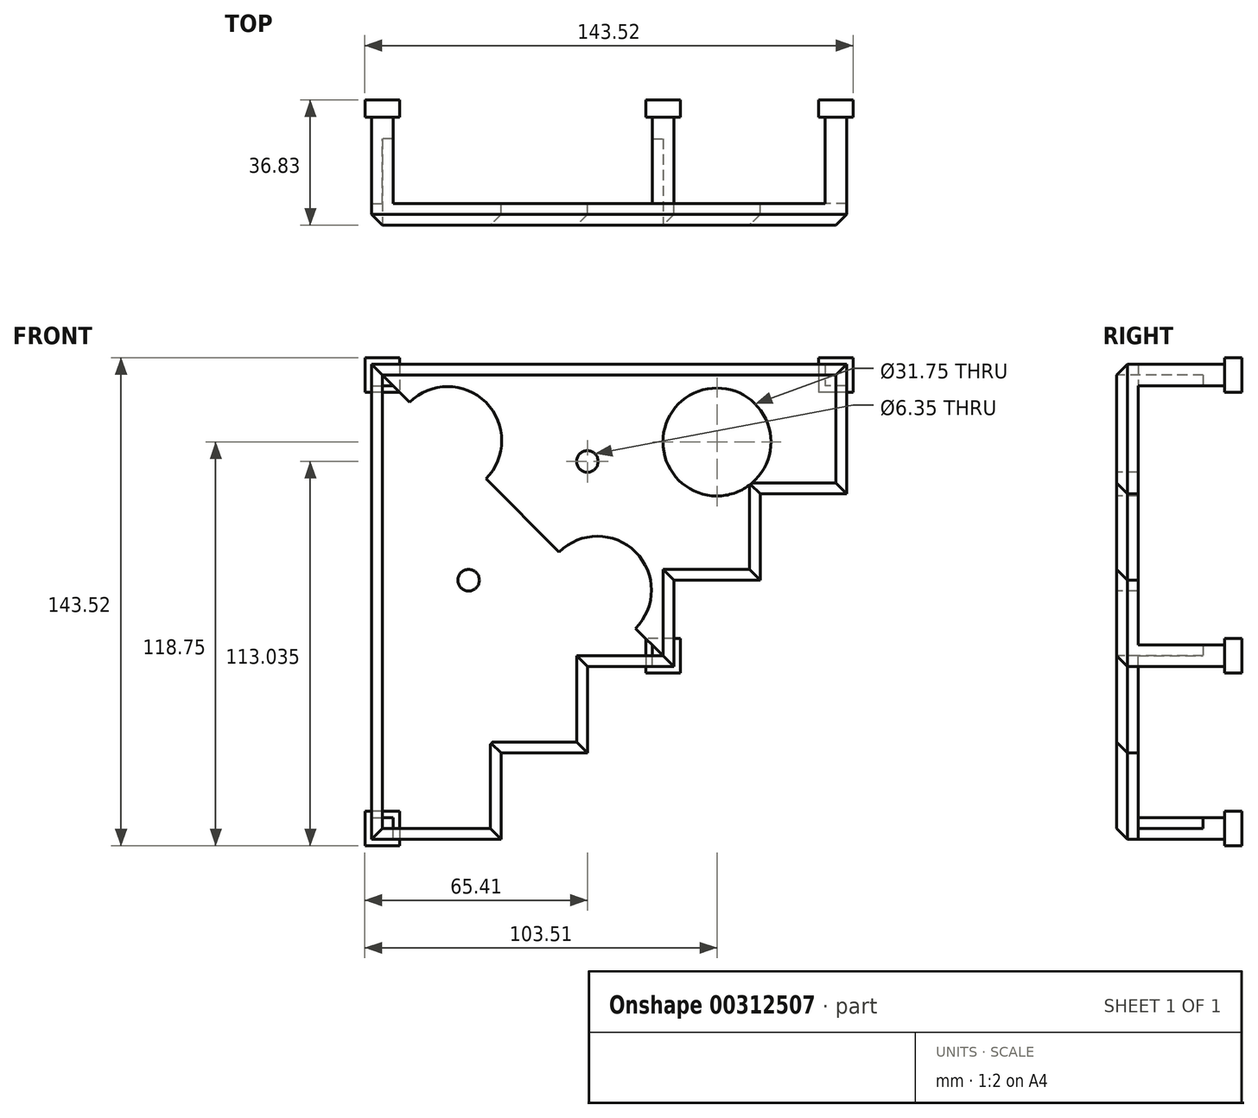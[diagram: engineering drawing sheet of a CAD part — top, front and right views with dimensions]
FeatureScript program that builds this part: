
annotation { "Feature Type Name" : "Feature", "Feature Type Description" : "" }
export const myFeature = defineFeature(function(context is Context, id is Id, definition is map)
    precondition{}
    {
        {
            var Q0;
            Q0=qCreatedBy(makeId("Front.planeOp"),FACE);
            var sketch = newSketch(context, id + "F0", { "sketchPlane" : qUnion([Q0])});
            skLineSegment(sketch, "E0", {"start": v(0, 0) * mm, "end": v(139.7, 0) * mm});
            skLineSegment(sketch, "E1", {"start": v(0, 0) * mm, "end": v(0, -139.7) * mm});
            skLineSegment(sketch, "E2", {"start": v(0, -139.7) * mm, "end": v(38.1, -139.7) * mm});
            skLineSegment(sketch, "E3", {"start": v(38.1, -139.7) * mm, "end": v(38.1, -114.3) * mm});
            skLineSegment(sketch, "E4", {"start": v(38.1, -114.3) * mm, "end": v(63.5, -114.3) * mm});
            skLineSegment(sketch, "E5", {"start": v(139.7, 0) * mm, "end": v(139.7, -38.1) * mm});
            skLineSegment(sketch, "E6", {"start": v(139.7, -38.1) * mm, "end": v(114.3, -38.1) * mm});
            skLineSegment(sketch, "E7", {"start": v(114.3, -38.1) * mm, "end": v(114.3, -63.5) * mm});
            skLineSegment(sketch, "E8", {"start": v(114.3, -63.5) * mm, "end": v(88.9, -63.5) * mm});
            skLineSegment(sketch, "E9", {"start": v(63.5, -114.3) * mm, "end": v(63.5, -88.9) * mm});
            skLineSegment(sketch, "E10", {"start": v(63.5, -88.9) * mm, "end": v(88.9, -88.9) * mm});
            skLineSegment(sketch, "E11", {"start": v(88.9, -88.9) * mm, "end": v(88.9, -63.5) * mm});
            skSolve(sketch);
        }
        {
            var Q0;
            Q0=makeQuery(id+"F0.imprint","IMPRINT",FACE,{"disambiguationData":[TD([[makeQuery(id+"F0.imprint","IMPRINT",EDGE,{"derivedFrom":sQuery(id+"F0.wireOp",EDGE,"E0")}),-1.0]])]});
            extrude(context, id + "F1", {"entities" : qUnion([Q0]), "depth" : 6.35 * mm});
        }
        {
            var Q0;
            Q0=makeQuery(id+"F1.opExtrude","CAP_FACE",FACE,{"disambiguationData":[OSD([sQuery(id+"F0.wireOp",EDGE,"E0"),sQuery(id+"F0.wireOp",EDGE,"E1"),sQuery(id+"F0.wireOp",EDGE,"E2"),sQuery(id+"F0.wireOp",EDGE,"E3"),sQuery(id+"F0.wireOp",EDGE,"E4"),sQuery(id+"F0.wireOp",EDGE,"E5"),sQuery(id+"F0.wireOp",EDGE,"E6"),sQuery(id+"F0.wireOp",EDGE,"E7"),sQuery(id+"F0.wireOp",EDGE,"E8"),sQuery(id+"F0.wireOp",EDGE,"E9"),sQuery(id+"F0.wireOp",EDGE,"E10"),sQuery(id+"F0.wireOp",EDGE,"E11")])],"isStart":false});
            var sketch = newSketch(context, id + "F2", { "sketchPlane" : qUnion([Q0])});
            skLineSegment(sketch, "E12.0", {"start": v(35.56, -19.05) * mm, "end": v(35.5, -19.05) * mm});
            skLineSegment(sketch, "E13", {"start": v(88.9, -88.9) * mm, "end": v(66.45, -66.45) * mm});
            skCircle(sketch, "E14", {"center": v(66.45, -66.45) * mm, "radius": 15.88 * mm});
            skLineSegment(sketch, "E15", {"start": v(0, 0) * mm, "end": v(22.45, -22.45) * mm});
            skCircle(sketch, "E16", {"center": v(22.45, -22.45) * mm, "radius": 15.88 * mm});
            skPoint(sketch, "E17.endSnap0", {"position": v(0, -69.85) * mm});
            skPoint(sketch, "E18.endSnap0", {"position": v(139.7, -19.05) * mm});
            skLineSegment(sketch, "E19", {"start": v(101.6, -63.5) * mm, "end": v(101.6, -22.86) * mm});
            skCircle(sketch, "E20", {"center": v(101.6, -22.86) * mm, "radius": 15.88 * mm});
            skLineSegment(sketch, "E21", {"start": v(101.6, -22.86) * mm, "end": v(139.7, -22.86) * mm});
            skLineSegment(sketch, "E22", {"start": v(63.5, -101.6) * mm, "end": v(22.86, -101.6) * mm});
            skCircle(sketch, "E23", {"center": v(22.86, -101.6) * mm, "radius": 15.88 * mm});
            skSolve(sketch);
        }
        {
            var Q0;
            Q0=makeQuery(id+"F1.opExtrude","CAP_EDGE",EDGE,{"disambiguationData":[OSD([sQuery(id+"F0.wireOp",EDGE,"E0")])],"isStart":false});
            var Q1;
            Q1=makeQuery(id+"F1.opExtrude","CAP_EDGE",EDGE,{"disambiguationData":[OSD([sQuery(id+"F0.wireOp",EDGE,"E1")])],"isStart":false});
            var Q2;
            Q2=makeQuery(id+"F1.opExtrude","CAP_EDGE",EDGE,{"disambiguationData":[OSD([sQuery(id+"F0.wireOp",EDGE,"E2")])],"isStart":false});
            var Q3;
            Q3=makeQuery(id+"F1.opExtrude","CAP_EDGE",EDGE,{"disambiguationData":[OSD([sQuery(id+"F0.wireOp",EDGE,"E3")])],"isStart":false});
            var Q4;
            Q4=makeQuery(id+"F1.opExtrude","CAP_FACE",FACE,{"disambiguationData":[OSD([sQuery(id+"F0.wireOp",EDGE,"E0"),sQuery(id+"F0.wireOp",EDGE,"E1"),sQuery(id+"F0.wireOp",EDGE,"E2"),sQuery(id+"F0.wireOp",EDGE,"E3"),sQuery(id+"F0.wireOp",EDGE,"E4"),sQuery(id+"F0.wireOp",EDGE,"E5"),sQuery(id+"F0.wireOp",EDGE,"E6"),sQuery(id+"F0.wireOp",EDGE,"E7"),sQuery(id+"F0.wireOp",EDGE,"E8"),sQuery(id+"F0.wireOp",EDGE,"E9"),sQuery(id+"F0.wireOp",EDGE,"E10"),sQuery(id+"F0.wireOp",EDGE,"E11")])],"isStart":false});
            chamfer(context, id + "F3", {"entities" : qUnion([Q0, Q1, Q2, Q3, Q4]), "width" : 3.17 * mm, "tangentPropagation" : true});
        }
        {
            var Q0;
            {var subQ0=sQuery(id+"F0.wireOp",EDGE,"E8");var subQ1=sQuery(id+"F0.wireOp",EDGE,"E7");var subQ2=sQuery(id+"F0.wireOp",EDGE,"E6");var subQ3=sQuery(id+"F0.wireOp",EDGE,"E5");var subQ4=sQuery(id+"F0.wireOp",EDGE,"E4");var subQ5=sQuery(id+"F0.wireOp",EDGE,"E3");var subQ6=sQuery(id+"F0.wireOp",EDGE,"E11");var subQ7=sQuery(id+"F0.wireOp",EDGE,"E10");var subQ8=sQuery(id+"F0.wireOp",EDGE,"E9");var subQ9=sQuery(id+"F0.wireOp",EDGE,"E2");var subQ10=sQuery(id+"F0.wireOp",EDGE,"E1");var subQ11=sQuery(id+"F0.wireOp",EDGE,"E0");var subQ12=makeQuery(id+"F1.opExtrude","CAP_FACE",FACE,{"disambiguationData":[OSD([subQ11,subQ10,subQ9,subQ5,subQ4,subQ3,subQ2,subQ1,subQ0,subQ8,subQ7,subQ6])],"isStart":false});Q0=makeQuery(id+"F9R2ZcsSHay4FVk_1.boolean.opBoolean","SPLIT",FACE,{"disambiguationData":[TD([subQ12,makeQuery(id+"F3.opChamfer","BLEND_FACE",FACE,{"disambiguationData":[OSD([subQ11])]}),makeQuery(id+"F3.opChamfer","BLEND_FACE",FACE,{"disambiguationData":[OSD([subQ10])]}),makeQuery(id+"F3.opChamfer","BLEND_FACE",FACE,{"disambiguationData":[OSD([subQ9])]}),makeQuery(id+"F3.opChamfer","BLEND_FACE",FACE,{"disambiguationData":[OSD([subQ5])]}),makeQuery(id+"F3.opChamfer","BLEND_FACE",FACE,{"disambiguationData":[OSD([subQ4])]}),makeQuery(id+"F3.opChamfer","BLEND_FACE",FACE,{"disambiguationData":[OSD([subQ3])]}),makeQuery(id+"F3.opChamfer","BLEND_FACE",FACE,{"disambiguationData":[OSD([subQ2])]}),makeQuery(id+"F3.opChamfer","BLEND_FACE",FACE,{"disambiguationData":[OSD([subQ1])]}),makeQuery(id+"F3.opChamfer","BLEND_FACE",FACE,{"disambiguationData":[OSD([subQ0])]}),makeQuery(id+"F3.opChamfer","BLEND_FACE",FACE,{"disambiguationData":[OSD([subQ8])]}),makeQuery(id+"F3.opChamfer","BLEND_FACE",FACE,{"disambiguationData":[OSD([subQ7])]}),makeQuery(id+"F3.opChamfer","BLEND_FACE",FACE,{"disambiguationData":[OSD([subQ6])]}),makeQuery(id+"F9R2ZcsSHay4FVk_1.opExtrude","SWEPT_FACE",FACE,{"disambiguationData":[OSD([sQuery(id+"F2.wireOp",EDGE,"RUFc5baY-S6u0-vs6P-XKJA-CRQodAUy7xYm")])]}),makeQuery(id+"F9R2ZcsSHay4FVk_1.opExtrude","SWEPT_FACE",FACE,{"disambiguationData":[OSD([sQuery(id+"F2.wireOp",EDGE,"YVMzEVT3-NPLW-DXTr-AYYg-EaG1P3SBG4JG")])]}),makeQuery(id+"F9R2ZcsSHay4FVk_1.opExtrude","SWEPT_FACE",FACE,{"disambiguationData":[OSD([sQuery(id+"F2.wireOp",EDGE,"fjYobeJb-4CdX-EGAB-SbWo-5lYiXrXiOomk")])]})])],"derivedFrom":subQ12});}
            var sketch = newSketch(context, id + "F4", { "sketchPlane" : qUnion([Q0])});
            skLineSegment(sketch, "E24", {"start": v(69.85, -3.17) * mm, "end": v(69.85, -28.58) * mm});
            skPoint(sketch, "E24.endSnap0", {"position": v(69.85, -3.17) * mm});
            skLineSegment(sketch, "E25", {"start": v(69.85, -28.58) * mm, "end": v(73.03, -28.58) * mm});
            skLineSegment(sketch, "E26", {"start": v(3.17, -3.17) * mm, "end": v(85.73, -85.73) * mm});
            skLineSegment(sketch, "E27", {"start": v(69.85, -28.58) * mm, "end": v(63.5, -28.58) * mm});
            skCircle(sketch, "E28", {"center": v(63.5, -28.58) * mm, "radius": 3.18 * mm});
            skCircle(sketch, "E29.MirrorC", {"center": v(28.58, -63.5) * mm, "radius": 3.18 * mm});
            skPoint(sketch, "E30.endSnap0", {"position": v(111.13, -47.63) * mm});
            skPoint(sketch, "E31.endSnap0", {"position": v(47.63, -111.13) * mm});
            skSolve(sketch);
        }
        {
            var Q0;
            Q0=makeQuery(id+"F1.opExtrude","CAP_FACE",FACE,{"disambiguationData":[OSD([sQuery(id+"F0.wireOp",EDGE,"E0"),sQuery(id+"F0.wireOp",EDGE,"E1"),sQuery(id+"F0.wireOp",EDGE,"E2"),sQuery(id+"F0.wireOp",EDGE,"E3"),sQuery(id+"F0.wireOp",EDGE,"E4"),sQuery(id+"F0.wireOp",EDGE,"E5"),sQuery(id+"F0.wireOp",EDGE,"E6"),sQuery(id+"F0.wireOp",EDGE,"E7"),sQuery(id+"F0.wireOp",EDGE,"E8"),sQuery(id+"F0.wireOp",EDGE,"E9"),sQuery(id+"F0.wireOp",EDGE,"E10"),sQuery(id+"F0.wireOp",EDGE,"E11")])],"isStart":true});
            var sketch = newSketch(context, id + "F5", { "sketchPlane" : qUnion([Q0])});
            skLineSegment(sketch, "E32.bottom", {"start": v(0, 0) * mm, "end": v(-6.35, 0) * mm});
            skLineSegment(sketch, "E32.top", {"start": v(0, -6.35) * mm, "end": v(-6.35, -6.35) * mm});
            skLineSegment(sketch, "E32.left", {"start": v(0, 0) * mm, "end": v(0, -6.35) * mm});
            skLineSegment(sketch, "E32.right", {"start": v(-6.35, 0) * mm, "end": v(-6.35, -6.35) * mm});
            skLineSegment(sketch, "E33.bottom", {"start": v(-139.7, 0) * mm, "end": v(-133.35, 0) * mm});
            skLineSegment(sketch, "E33.top", {"start": v(-139.7, -6.35) * mm, "end": v(-133.35, -6.35) * mm});
            skLineSegment(sketch, "E33.left", {"start": v(-139.7, 0) * mm, "end": v(-139.7, -6.35) * mm});
            skLineSegment(sketch, "E33.right", {"start": v(-133.35, 0) * mm, "end": v(-133.35, -6.35) * mm});
            skLineSegment(sketch, "E34.bottom", {"start": v(-88.9, -88.9) * mm, "end": v(-82.55, -88.9) * mm});
            skLineSegment(sketch, "E34.top", {"start": v(-88.9, -82.55) * mm, "end": v(-82.55, -82.55) * mm});
            skLineSegment(sketch, "E34.left", {"start": v(-88.9, -88.9) * mm, "end": v(-88.9, -82.55) * mm});
            skLineSegment(sketch, "E34.right", {"start": v(-82.55, -88.9) * mm, "end": v(-82.55, -82.55) * mm});
            skLineSegment(sketch, "E35.bottom", {"start": v(0, -139.7) * mm, "end": v(-6.35, -139.7) * mm});
            skLineSegment(sketch, "E35.top", {"start": v(0, -133.35) * mm, "end": v(-6.35, -133.35) * mm});
            skLineSegment(sketch, "E35.left", {"start": v(0, -139.7) * mm, "end": v(0, -133.35) * mm});
            skLineSegment(sketch, "E35.right", {"start": v(-6.35, -139.7) * mm, "end": v(-6.35, -133.35) * mm});
            skSolve(sketch);
        }
        {
            var Q0;
            Q0=makeQuery(id+"F5.imprint","IMPRINT",FACE,{"disambiguationData":[TD([[makeQuery(id+"F5.imprint","IMPRINT",EDGE,{"derivedFrom":sQuery(id+"F5.wireOp",EDGE,"E32.bottom")}),1.0]])]});
            var Q1;
            Q1=makeQuery(id+"F5.imprint","IMPRINT",FACE,{"disambiguationData":[TD([[makeQuery(id+"F5.imprint","IMPRINT",EDGE,{"derivedFrom":sQuery(id+"F5.wireOp",EDGE,"E35.bottom")}),-1.0]])]});
            var Q2;
            Q2=makeQuery(id+"F5.imprint","IMPRINT",FACE,{"disambiguationData":[TD([[makeQuery(id+"F5.imprint","IMPRINT",EDGE,{"derivedFrom":sQuery(id+"F5.wireOp",EDGE,"hBAFwnPM-8Qk3-NIPh-aYN5-VEe4ey89t3Te.bottom")}),-1.0]])]});
            var Q3;
            Q3=makeQuery(id+"F5.imprint","IMPRINT",FACE,{"disambiguationData":[TD([[makeQuery(id+"F5.imprint","IMPRINT",EDGE,{"derivedFrom":sQuery(id+"F5.wireOp",EDGE,"wdLdXJvT-cpnT-Piy2-WavO-D7dy1cOLv9jC.bottom")}),-1.0]])]});
            var Q4;
            Q4=makeQuery(id+"F5.imprint","IMPRINT",FACE,{"disambiguationData":[TD([[makeQuery(id+"F5.imprint","IMPRINT",EDGE,{"derivedFrom":sQuery(id+"F5.wireOp",EDGE,"E34.bottom")}),-1.0]])]});
            var Q5;
            Q5=makeQuery(id+"F5.imprint","IMPRINT",FACE,{"disambiguationData":[TD([[makeQuery(id+"F5.imprint","IMPRINT",EDGE,{"derivedFrom":sQuery(id+"F5.wireOp",EDGE,"gIOO070n-KM1T-UyZ6-ehrV-S670dawngJGZ.bottom")}),1.0]])]});
            var Q6;
            Q6=makeQuery(id+"F5.imprint","IMPRINT",FACE,{"disambiguationData":[TD([[makeQuery(id+"F5.imprint","IMPRINT",EDGE,{"derivedFrom":sQuery(id+"F5.wireOp",EDGE,"YckFK4Ei-NoMX-VchO-rRQ0-DcAXENcsdehc.bottom")}),1.0]])]});
            var Q7;
            Q7=makeQuery(id+"F5.imprint","IMPRINT",FACE,{"disambiguationData":[TD([[makeQuery(id+"F5.imprint","IMPRINT",EDGE,{"derivedFrom":sQuery(id+"F5.wireOp",EDGE,"E33.bottom")}),1.0]])]});
            extrude(context, id + "F6", {"entities" : qUnion([Q0, Q1, Q2, Q3, Q4, Q5, Q6, Q7]), "operationType" : NewBodyOperationType.ADD, "depth" : 25.4 * mm, "offsetDistance" : 25.4 * mm});
        }
        {
            var Q0;
            {var subQ0=sQuery(id+"F2.wireOp",EDGE,"E21");var subQ1=sQuery(id+"F2.wireOp",EDGE,"E19");var subQ2=makeQuery(id+"F2.imprint","INTERSECT",VERTEX,{"derivedFrom":[subQ1,subQ0]});Q0=makeQuery(id+"F2.imprint","IMPRINT",FACE,{"disambiguationData":[TD([[makeQuery(id+"F2.imprint","IMPRINT",EDGE,{"disambiguationData":[TD([[subQ2,1.0]])],"derivedFrom":subQ1}),1.0]])]});}
            var Q1;
            {var subQ0=sQuery(id+"F2.wireOp",EDGE,"E21");var subQ1=sQuery(id+"F2.wireOp",EDGE,"E19");var subQ2=makeQuery(id+"F2.imprint","INTERSECT",VERTEX,{"derivedFrom":[subQ1,subQ0]});Q1=makeQuery(id+"F2.imprint","IMPRINT",FACE,{"disambiguationData":[TD([[makeQuery(id+"F2.imprint","IMPRINT",EDGE,{"disambiguationData":[TD([[subQ2,1.0]])],"derivedFrom":subQ1}),-1.0]])]});}
            var Q2;
            Q2=makeQuery(id+"F2.imprint","IMPRINT",FACE,{"disambiguationData":[TD([[makeQuery(id+"F2.imprint","IMPRINT",EDGE,{"derivedFrom":sQuery(id+"F2.wireOp",EDGE,"E14")}),1.0]])]});
            var Q3;
            Q3=makeQuery(id+"F2.imprint","IMPRINT",FACE,{"disambiguationData":[TD([[makeQuery(id+"F2.imprint","IMPRINT",EDGE,{"derivedFrom":sQuery(id+"F2.wireOp",EDGE,"E23")}),1.0]])]});
            var Q4;
            Q4=makeQuery(id+"F2.imprint","IMPRINT",FACE,{"disambiguationData":[TD([[makeQuery(id+"F2.imprint","IMPRINT",EDGE,{"derivedFrom":sQuery(id+"F2.wireOp",EDGE,"E16")}),1.0]])]});
            extrude(context, id + "F7", {"entities" : qUnion([Q0, Q1, Q2, Q3, Q4]), "operationType" : NewBodyOperationType.REMOVE, "oppositeDirection" : true, "depth" : 25.4 * mm});
        }
        {
            var Q0;
            Q0=makeQuery(id+"F6.opExtrude","CAP_FACE",FACE,{"disambiguationData":[OSD([sQuery(id+"F5.wireOp",EDGE,"E32.bottom"),sQuery(id+"F5.wireOp",EDGE,"E32.top"),sQuery(id+"F5.wireOp",EDGE,"E32.left"),sQuery(id+"F5.wireOp",EDGE,"E32.right")])],"isStart":false});
            var sketch = newSketch(context, id + "F8", { "sketchPlane" : qUnion([Q0])});
            skLineSegment(sketch, "E36.bottom", {"start": v(-8.26, 1.9) * mm, "end": v(1.9, 1.9) * mm});
            skLineSegment(sketch, "E36.top", {"start": v(-8.26, -8.26) * mm, "end": v(1.9, -8.26) * mm});
            skLineSegment(sketch, "E36.left", {"start": v(-8.26, 1.9) * mm, "end": v(-8.26, -8.26) * mm});
            skLineSegment(sketch, "E36.right", {"start": v(1.9, 1.9) * mm, "end": v(1.9, -8.26) * mm});
            skPoint(sketch, "E36.middle", {"position": v(-3.17, -3.17) * mm});
            skPoint(sketch, "E36.middle.positionSnap0", {"position": v(0, -3.17) * mm});
            skPoint(sketch, "E36.middle.positionSnap1", {"position": v(-3.17, -6.35) * mm});
            skPoint(sketch, "E36.centerSnap0", {"position": v(0, -3.17) * mm});
            skPoint(sketch, "E36.centerSnap1", {"position": v(-3.17, -6.35) * mm});
            skSolve(sketch);
        }
        {
            var Q0;
            Q0=makeQuery(id+"F8.imprint","IMPRINT",FACE,{"disambiguationData":[TD([[makeQuery(id+"F8.imprint","IMPRINT",EDGE,{"derivedFrom":sQuery(id+"F8.wireOp",EDGE,"E36.bottom")}),-1.0]])]});
            var Q1;
            Q1=makeQuery(id+"F8.imprint","IMPRINT",FACE,{"disambiguationData":[TD([[makeQuery(id+"F8.imprint","IMPRINT",EDGE,{"derivedFrom":makeQuery(id+"F6.opExtrude","CAP_EDGE",EDGE,{"disambiguationData":[OSD([sQuery(id+"F5.wireOp",EDGE,"E32.bottom")])],"isStart":false})}),1.0]])]});
            extrude(context, id + "F9", {"entities" : qUnion([Q0, Q1]), "operationType" : NewBodyOperationType.ADD, "depth" : 5.08 * mm, "offsetDistance" : 25.4 * mm});
        }
        {
            var Q0;
            Q0=makeQuery(id+"F6.opExtrude","CAP_FACE",FACE,{"disambiguationData":[OSD([sQuery(id+"F5.wireOp",EDGE,"E33.bottom"),sQuery(id+"F5.wireOp",EDGE,"E33.top"),sQuery(id+"F5.wireOp",EDGE,"E33.left"),sQuery(id+"F5.wireOp",EDGE,"E33.right")])],"isStart":false});
            var sketch = newSketch(context, id + "F10", { "sketchPlane" : qUnion([Q0])});
            skLineSegment(sketch, "E37.bottom", {"start": v(-141.6, 1.9) * mm, "end": v(-131.44, 1.9) * mm});
            skLineSegment(sketch, "E37.top", {"start": v(-141.6, -8.26) * mm, "end": v(-131.44, -8.26) * mm});
            skLineSegment(sketch, "E37.left", {"start": v(-141.6, 1.9) * mm, "end": v(-141.6, -8.26) * mm});
            skLineSegment(sketch, "E37.right", {"start": v(-131.44, 1.9) * mm, "end": v(-131.44, -8.26) * mm});
            skPoint(sketch, "E37.middle", {"position": v(-136.53, -3.17) * mm});
            skPoint(sketch, "E37.middle.positionSnap0", {"position": v(-133.35, -3.17) * mm});
            skPoint(sketch, "E37.middle.positionSnap1", {"position": v(-136.53, -6.35) * mm});
            skPoint(sketch, "E37.centerSnap0", {"position": v(-133.35, -3.17) * mm});
            skPoint(sketch, "E37.centerSnap1", {"position": v(-136.53, -6.35) * mm});
            skSolve(sketch);
        }
        {
            var Q0;
            Q0=makeQuery(id+"F10.imprint","IMPRINT",FACE,{"disambiguationData":[TD([[makeQuery(id+"F10.imprint","IMPRINT",EDGE,{"derivedFrom":sQuery(id+"F10.wireOp",EDGE,"E37.bottom")}),-1.0]])]});
            var Q1;
            Q1=makeQuery(id+"F10.imprint","IMPRINT",FACE,{"disambiguationData":[TD([[makeQuery(id+"F10.imprint","IMPRINT",EDGE,{"derivedFrom":makeQuery(id+"F6.opExtrude","CAP_EDGE",EDGE,{"disambiguationData":[OSD([sQuery(id+"F5.wireOp",EDGE,"E33.bottom")])],"isStart":false})}),1.0]])]});
            extrude(context, id + "F11", {"entities" : qUnion([Q0, Q1]), "operationType" : NewBodyOperationType.ADD, "depth" : 5.08 * mm, "offsetDistance" : 25.4 * mm});
        }
        {
            var Q0;
            Q0=makeQuery(id+"F6.opExtrude","CAP_FACE",FACE,{"disambiguationData":[OSD([sQuery(id+"F5.wireOp",EDGE,"E34.bottom"),sQuery(id+"F5.wireOp",EDGE,"E34.top"),sQuery(id+"F5.wireOp",EDGE,"E34.left"),sQuery(id+"F5.wireOp",EDGE,"E34.right")])],"isStart":false});
            var sketch = newSketch(context, id + "F12", { "sketchPlane" : qUnion([Q0])});
            skLineSegment(sketch, "E38.bottom", {"start": v(-90.8, -80.65) * mm, "end": v(-80.65, -80.65) * mm});
            skLineSegment(sketch, "E38.top", {"start": v(-90.8, -90.8) * mm, "end": v(-80.65, -90.8) * mm});
            skLineSegment(sketch, "E38.left", {"start": v(-90.8, -80.65) * mm, "end": v(-90.8, -90.8) * mm});
            skLineSegment(sketch, "E38.right", {"start": v(-80.65, -80.65) * mm, "end": v(-80.65, -90.8) * mm});
            skPoint(sketch, "E38.middle", {"position": v(-85.73, -85.73) * mm});
            skPoint(sketch, "E38.middle.positionSnap0", {"position": v(-88.9, -85.73) * mm});
            skPoint(sketch, "E38.middle.positionSnap1", {"position": v(-85.73, -82.55) * mm});
            skPoint(sketch, "E38.centerSnap0", {"position": v(-88.9, -85.73) * mm});
            skPoint(sketch, "E38.centerSnap1", {"position": v(-85.73, -82.55) * mm});
            skSolve(sketch);
        }
        {
            var Q0;
            Q0=makeQuery(id+"F12.imprint","IMPRINT",FACE,{"disambiguationData":[TD([[makeQuery(id+"F12.imprint","IMPRINT",EDGE,{"derivedFrom":makeQuery(id+"F6.opExtrude","CAP_EDGE",EDGE,{"disambiguationData":[OSD([sQuery(id+"F5.wireOp",EDGE,"E34.bottom")])],"isStart":false})}),-1.0]])]});
            var Q1;
            Q1=makeQuery(id+"F12.imprint","IMPRINT",FACE,{"disambiguationData":[TD([[makeQuery(id+"F12.imprint","IMPRINT",EDGE,{"derivedFrom":sQuery(id+"F12.wireOp",EDGE,"E38.bottom")}),-1.0]])]});
            extrude(context, id + "F13", {"entities" : qUnion([Q0, Q1]), "operationType" : NewBodyOperationType.ADD, "depth" : 5.08 * mm, "offsetDistance" : 25.4 * mm});
        }
        {
            var Q0;
            Q0=makeQuery(id+"F6.opExtrude","CAP_FACE",FACE,{"disambiguationData":[OSD([sQuery(id+"F5.wireOp",EDGE,"E35.bottom"),sQuery(id+"F5.wireOp",EDGE,"E35.top"),sQuery(id+"F5.wireOp",EDGE,"E35.left"),sQuery(id+"F5.wireOp",EDGE,"E35.right")])],"isStart":false});
            var sketch = newSketch(context, id + "F14", { "sketchPlane" : qUnion([Q0])});
            skLineSegment(sketch, "E39.bottom", {"start": v(-8.26, -131.44) * mm, "end": v(1.9, -131.44) * mm});
            skLineSegment(sketch, "E39.top", {"start": v(-8.26, -141.6) * mm, "end": v(1.9, -141.6) * mm});
            skLineSegment(sketch, "E39.left", {"start": v(-8.26, -131.44) * mm, "end": v(-8.26, -141.6) * mm});
            skLineSegment(sketch, "E39.right", {"start": v(1.9, -131.44) * mm, "end": v(1.9, -141.6) * mm});
            skPoint(sketch, "E39.middle", {"position": v(-3.18, -136.53) * mm});
            skPoint(sketch, "E39.middle.positionSnap0", {"position": v(-6.35, -136.53) * mm});
            skPoint(sketch, "E39.middle.positionSnap1", {"position": v(-3.18, -133.35) * mm});
            skPoint(sketch, "E39.centerSnap0", {"position": v(-6.35, -136.53) * mm});
            skPoint(sketch, "E39.centerSnap1", {"position": v(-3.18, -133.35) * mm});
            skSolve(sketch);
        }
        {
            var Q0;
            Q0=makeQuery(id+"F14.imprint","IMPRINT",FACE,{"disambiguationData":[TD([[makeQuery(id+"F14.imprint","IMPRINT",EDGE,{"derivedFrom":makeQuery(id+"F6.opExtrude","CAP_EDGE",EDGE,{"disambiguationData":[OSD([sQuery(id+"F5.wireOp",EDGE,"E35.bottom")])],"isStart":false})}),-1.0]])]});
            var Q1;
            Q1=makeQuery(id+"F14.imprint","IMPRINT",FACE,{"disambiguationData":[TD([[makeQuery(id+"F14.imprint","IMPRINT",EDGE,{"derivedFrom":sQuery(id+"F14.wireOp",EDGE,"E39.bottom")}),-1.0]])]});
            extrude(context, id + "F15", {"entities" : qUnion([Q0, Q1]), "operationType" : NewBodyOperationType.ADD, "depth" : 5.08 * mm, "offsetDistance" : 25.4 * mm});
        }
        {
            var Q0;
            Q0=makeQuery(id+"F4.imprint","IMPRINT",FACE,{"disambiguationData":[TD([[makeQuery(id+"F4.imprint","IMPRINT",EDGE,{"derivedFrom":sQuery(id+"F4.wireOp",EDGE,"E28")}),1.0]])]});
            var Q1;
            Q1=makeQuery(id+"F4.imprint","IMPRINT",FACE,{"disambiguationData":[TD([[makeQuery(id+"F4.imprint","IMPRINT",EDGE,{"derivedFrom":sQuery(id+"F4.wireOp",EDGE,"0Fip78gP-2jli-x5bN-isH2-kMjmRuVlBjkm")}),1.0]])]});
            var Q2;
            Q2=makeQuery(id+"F4.imprint","IMPRINT",FACE,{"disambiguationData":[TD([[makeQuery(id+"F4.imprint","IMPRINT",EDGE,{"derivedFrom":sQuery(id+"F4.wireOp",EDGE,"E29.MirrorC")}),-1.0]])]});
            var Q3;
            Q3=makeQuery(id+"F4.imprint","IMPRINT",FACE,{"disambiguationData":[TD([[makeQuery(id+"F4.imprint","IMPRINT",EDGE,{"derivedFrom":sQuery(id+"F4.wireOp",EDGE,"v2NCKPBO-ElTB-LFZP-21Mo-pdEXbHBaDt01")}),1.0]])]});
            extrude(context, id + "F16", {"entities" : qUnion([Q0, Q1, Q2, Q3]), "operationType" : NewBodyOperationType.REMOVE, "oppositeDirection" : true, "depth" : 25.4 * mm, "offsetDistance" : 25.4 * mm});
        }
    });
